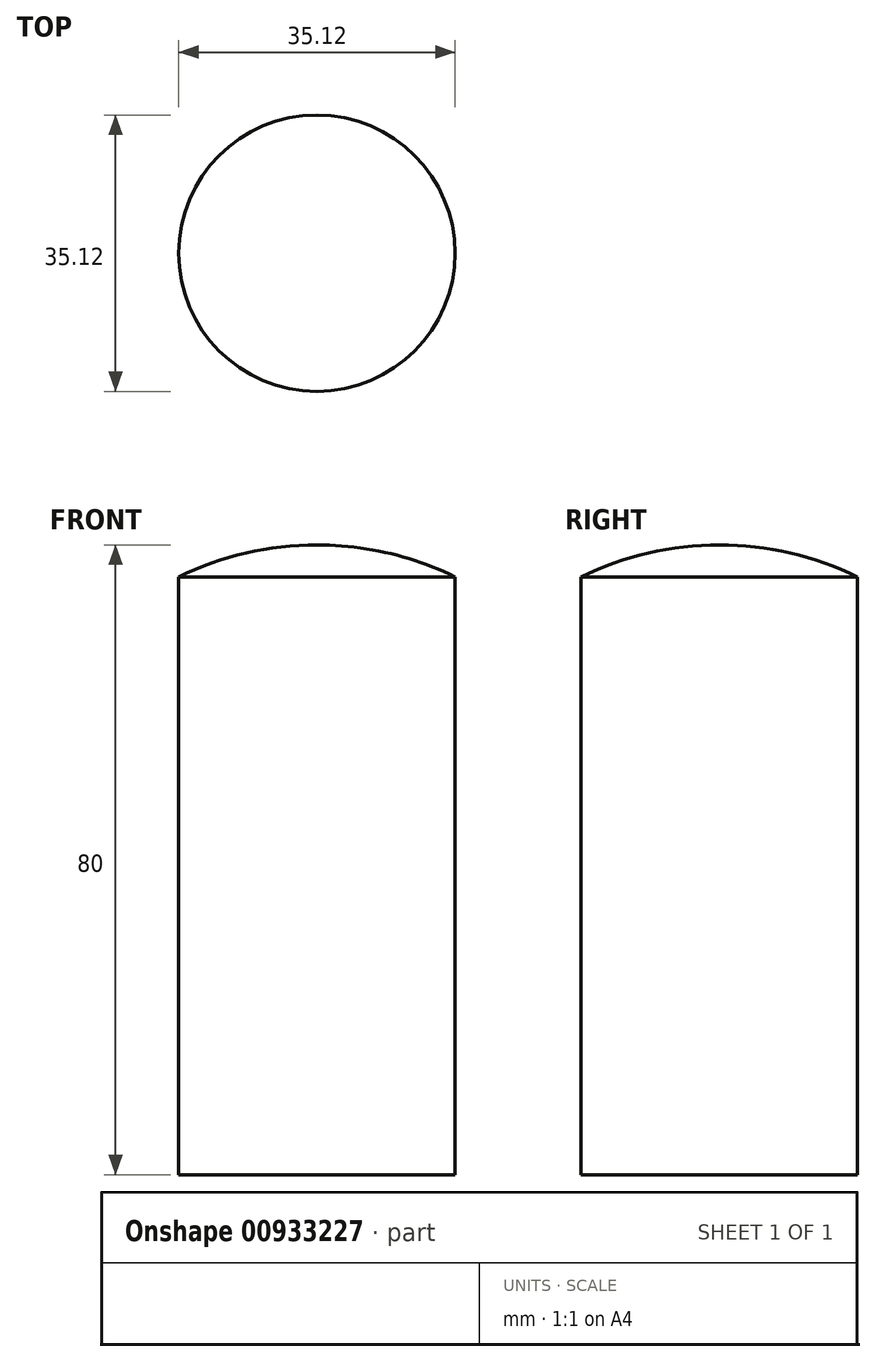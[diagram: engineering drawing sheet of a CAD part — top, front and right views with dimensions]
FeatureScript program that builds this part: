
annotation { "Feature Type Name" : "Feature", "Feature Type Description" : "" }
export const myFeature = defineFeature(function(context is Context, id is Id, definition is map)
    precondition{}
    {
        {
            var Q0;
            Q0=qCreatedBy(makeId("Front.planeOp"),FACE);
            var sketch = newSketch(context, id + "F0", { "sketchPlane" : qUnion([Q0])});
            skLineSegment(sketch, "E0", {"start": v(0, -46.2) * mm, "end": v(17.56, -46.2) * mm});
            skLineSegment(sketch, "E1", {"start": v(17.56, -46.2) * mm, "end": v(17.56, 23.8) * mm});
            skLineSegment(sketch, "E2", {"start": v(0, -46.2) * mm, "end": v(0, 33.8) * mm});
            skCircle(sketch, "E3", {"center": v(0, -6.2) * mm, "radius": 40 * mm});
            skLineSegment(sketch, "E4", {"start": v(17.56, 23.8) * mm, "end": v(17.56, 29.75) * mm});
            skSolve(sketch);
        }
        {
            var Q0;
            {var subQ1=sQuery(id+"F0.wireOp",EDGE,"E2");Q0=makeQuery(id+"F0.imprint","IMPRINT",FACE,{"disambiguationData":[TD([[makeQuery(id+"F0.imprint","IMPRINT",EDGE,{"derivedFrom":subQ1}),-1.0]])]});}
            var Q1;
            {var subQ0=sQuery(id+"F0.wireOp",EDGE,"E0");Q1=makeQuery(id+"F0.imprint","IMPRINT",FACE,{"disambiguationData":[TD([[makeQuery(id+"F0.imprint","IMPRINT",EDGE,{"derivedFrom":subQ0}),1.0]])]});}
            var Q2;
            Q2=sQuery(id+"F0.wireOp",EDGE,"E2");
            revolve(context, id + "F1", {"surfaceOperationType" : NewSurfaceOperationType.NEW, "entities" : qUnion([Q0, Q1]), "axis" : qUnion([Q2]), "revolveType" : RevolveType.FULL});
        }
    });
